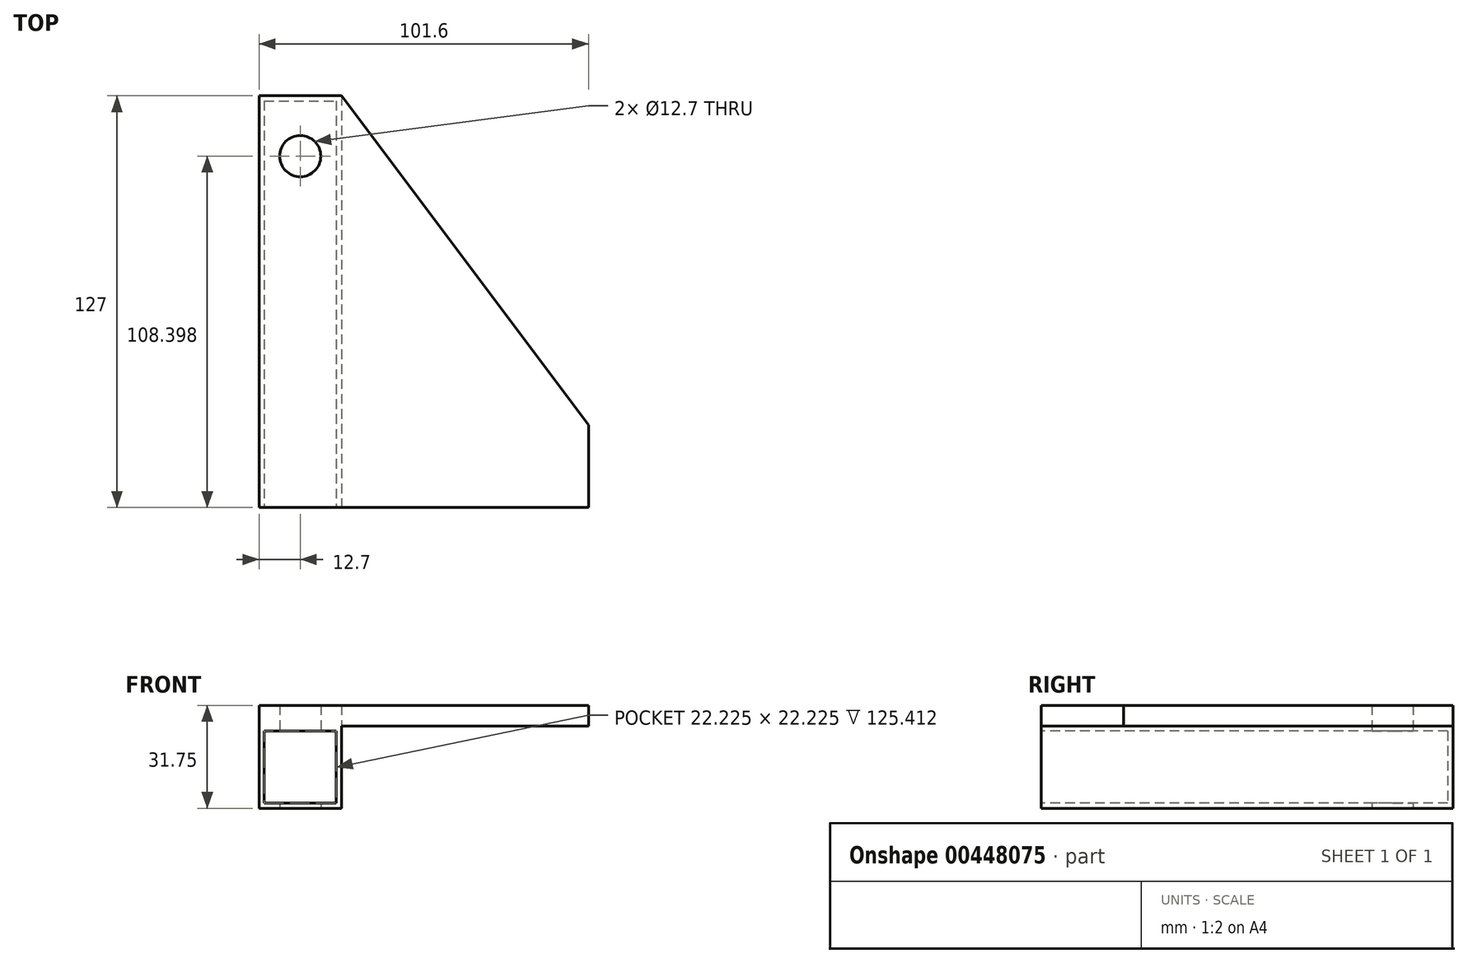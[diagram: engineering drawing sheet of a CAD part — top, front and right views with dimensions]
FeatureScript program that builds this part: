
annotation { "Feature Type Name" : "Feature", "Feature Type Description" : "" }
export const myFeature = defineFeature(function(context is Context, id is Id, definition is map)
    precondition{}
    {
        {
            var Q0;
            Q0=qCreatedBy(makeId("Top.planeOp"),FACE);
            var sketch = newSketch(context, id + "F0", { "sketchPlane" : qUnion([Q0])});
            skLineSegment(sketch, "E0.bottom", {"start": v(-12.7, 63.5) * mm, "end": v(12.7, 63.5) * mm});
            skLineSegment(sketch, "E0.top", {"start": v(-12.7, -63.5) * mm, "end": v(12.7, -63.5) * mm});
            skLineSegment(sketch, "E0.left", {"start": v(-12.7, 63.5) * mm, "end": v(-12.7, -63.5) * mm});
            skLineSegment(sketch, "E0.right", {"start": v(12.7, 63.5) * mm, "end": v(12.7, -63.5) * mm});
            skPoint(sketch, "E0.middle", {"position": v(0, 0) * mm});
            skSolve(sketch);
        }
        {
            var Q0;
            Q0 = qSketchRegion(id + "F0", true);
            extrude(context, id + "F1", {"entities" : qUnion([Q0]), "depth" : 25.4 * mm});
        }
        {
            var Q0;
            Q0=makeQuery(id+"F1.opExtrude","SWEPT_FACE",FACE,{"disambiguationData":[OSD([sQuery(id+"F0.wireOp",EDGE,"E0.top")])]});
            shell(context, id + "F2", {"entities" : qUnion([Q0]), "thickness" : 1.59 * mm});
        }
        {
            var Q0;
            Q0=makeQuery(id+"F1.opExtrude","CAP_FACE",FACE,{"disambiguationData":[OSD([sQuery(id+"F0.wireOp",EDGE,"E0.bottom"),sQuery(id+"F0.wireOp",EDGE,"E0.top"),sQuery(id+"F0.wireOp",EDGE,"E0.left"),sQuery(id+"F0.wireOp",EDGE,"E0.right")])],"isStart":false});
            var sketch = newSketch(context, id + "F3", { "sketchPlane" : qUnion([Q0])});
            skLineSegment(sketch, "E1.bottom", {"start": v(-12.7, 63.5) * mm, "end": v(12.7, 63.5) * mm});
            skLineSegment(sketch, "E1.top", {"start": v(-12.7, -63.5) * mm, "end": v(12.7, -63.5) * mm});
            skLineSegment(sketch, "E1.left", {"start": v(-12.7, 63.5) * mm, "end": v(-12.7, -63.5) * mm});
            skLineSegment(sketch, "E1.right", {"start": v(12.7, 63.5) * mm, "end": v(12.7, -63.5) * mm});
            skLineSegment(sketch, "E2.bottom", {"start": v(12.7, 63.5) * mm, "end": v(88.9, 63.5) * mm});
            skLineSegment(sketch, "E2.top", {"start": v(12.7, -63.5) * mm, "end": v(88.9, -63.5) * mm});
            skLineSegment(sketch, "E2.right", {"start": v(88.9, 63.5) * mm, "end": v(88.9, -63.5) * mm});
            skLineSegment(sketch, "E3", {"start": v(12.7, 63.5) * mm, "end": v(88.9, -38.1) * mm});
            skSolve(sketch);
        }
        {
            var Q0;
            Q0=makeQuery(id+"F3.imprint","IMPRINT",FACE,{"disambiguationData":[TD([[makeQuery(id+"F3.imprint","IMPRINT",EDGE,{"derivedFrom":sQuery(id+"F3.wireOp",EDGE,"E1.bottom")}),-1.0]])]});
            var Q1;
            {var subQ0=sQuery(id+"F3.wireOp",EDGE,"E2.top");Q1=makeQuery(id+"F3.imprint","IMPRINT",FACE,{"disambiguationData":[TD([[makeQuery(id+"F3.imprint","IMPRINT",EDGE,{"derivedFrom":subQ0}),1.0]])]});}
            extrude(context, id + "F4", {"entities" : qUnion([Q0, Q1]), "operationType" : NewBodyOperationType.ADD, "depth" : 6.35 * mm});
        }
        {
            var Q0;
            Q0=makeQuery(id+"F1.opExtrude","CAP_FACE",FACE,{"disambiguationData":[OSD([sQuery(id+"F0.wireOp",EDGE,"E0.bottom"),sQuery(id+"F0.wireOp",EDGE,"E0.top"),sQuery(id+"F0.wireOp",EDGE,"E0.left"),sQuery(id+"F0.wireOp",EDGE,"E0.right")])],"isStart":true});
            var sketch = newSketch(context, id + "F5", { "sketchPlane" : qUnion([Q0])});
            skCircle(sketch, "E4", {"center": v(0, -44.9) * mm, "radius": 6.35 * mm});
            skPoint(sketch, "E4.centerSnap0", {"position": v(0, -63.5) * mm});
            skCircle(sketch, "E5.cCircle", {"center": v(0, -44.9) * mm, "radius": 6.35 * mm, "construction": true});
            skPoint(sketch, "E5.0.midPoint", {"position": v(0, -38.55) * mm});
            skSolve(sketch);
        }
        {
            var Q0;
            Q0 = qSketchRegion(id + "F5", true);
            extrude(context, id + "F6", {"entities" : qUnion([Q0]), "operationType" : NewBodyOperationType.REMOVE, "endBound" : BoundingType.THROUGH_ALL, "oppositeDirection" : true, "depth" : 25.4 * mm});
        }
    });
